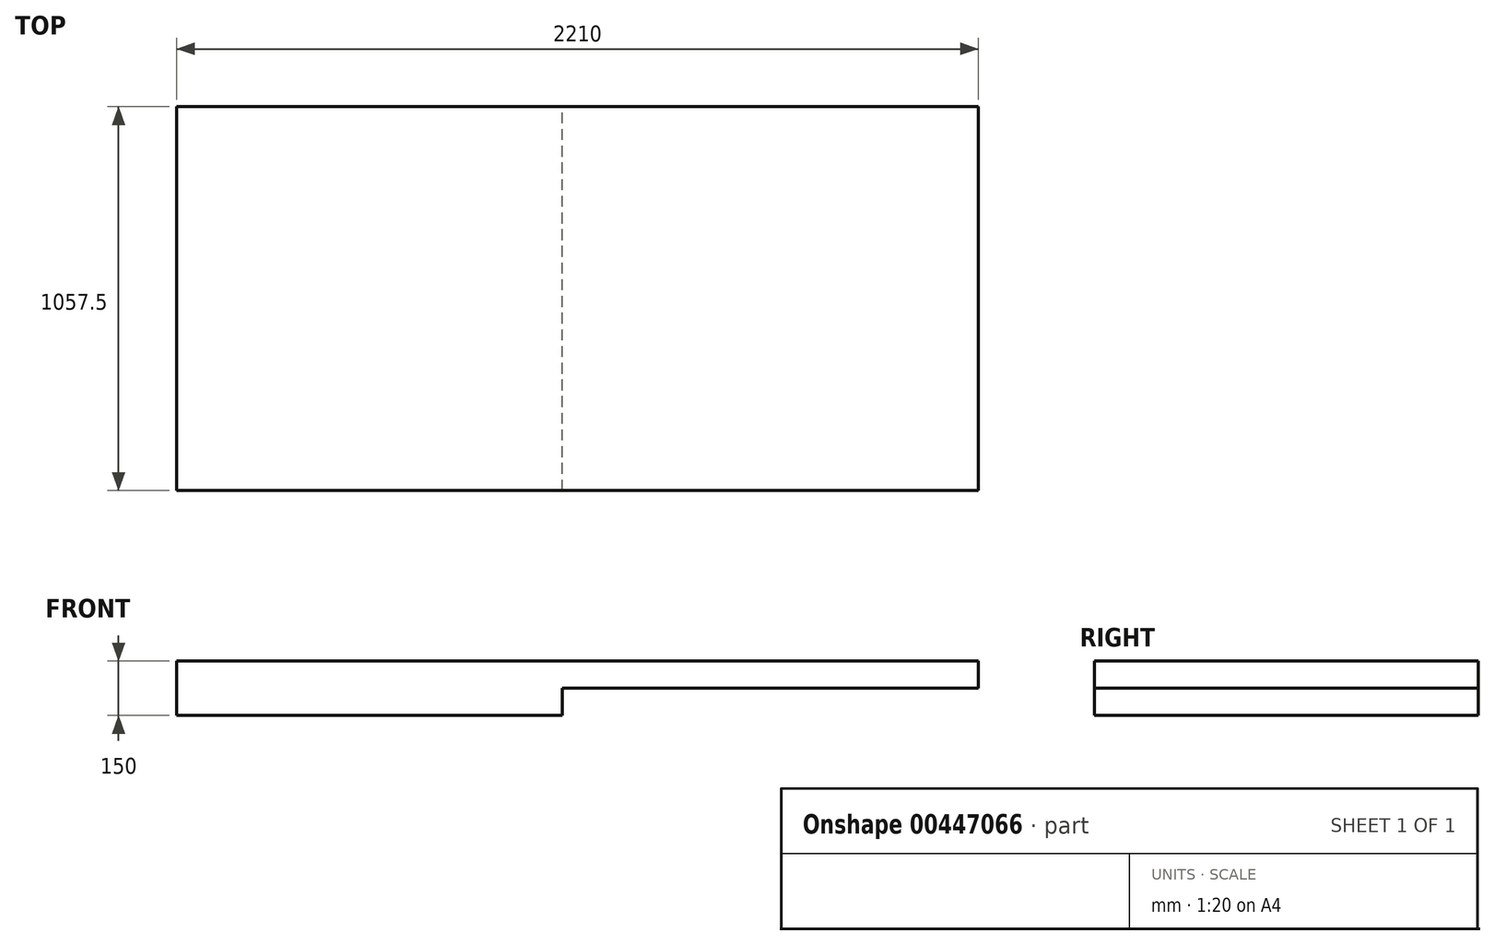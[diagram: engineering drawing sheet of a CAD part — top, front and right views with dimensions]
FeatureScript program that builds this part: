
annotation { "Feature Type Name" : "Feature", "Feature Type Description" : "" }
export const myFeature = defineFeature(function(context is Context, id is Id, definition is map)
    precondition{}
    {
        {
            var Q0;
            Q0=qCreatedBy(makeId("Top.planeOp"),FACE);
            var sketch = newSketch(context, id + "F0", { "sketchPlane" : qUnion([Q0])});
            skLineSegment(sketch, "E0.bottom", {"start": v(0, 0) * mm, "end": v(2210, 0) * mm});
            skLineSegment(sketch, "E0.top", {"start": v(0, 1057.5) * mm, "end": v(2210, 1057.5) * mm});
            skLineSegment(sketch, "E0.left", {"start": v(0, 0) * mm, "end": v(0, 1057.5) * mm});
            skLineSegment(sketch, "E0.right", {"start": v(2210, 0) * mm, "end": v(2210, 1057.5) * mm});
            skSolve(sketch);
        }
        {
            var Q0;
            Q0=makeQuery(id+"F0.imprint","IMPRINT",FACE,{"disambiguationData":[TD([[makeQuery(id+"F0.imprint","IMPRINT",EDGE,{"derivedFrom":sQuery(id+"F0.wireOp",EDGE,"E0.bottom")}),1.0]])]});
            extrude(context, id + "F1", {"entities" : qUnion([Q0]), "depth" : (65 * 2 + 20) * mm, "offsetDistance" : 25 * mm});
        }
        {
            var Q0;
            Q0=makeQuery(id+"F1.opExtrude","CAP_FACE",FACE,{"disambiguationData":[OSD([sQuery(id+"F0.wireOp",EDGE,"E0.bottom"),sQuery(id+"F0.wireOp",EDGE,"E0.top"),sQuery(id+"F0.wireOp",EDGE,"E0.left"),sQuery(id+"F0.wireOp",EDGE,"E0.right")])],"isStart":true});
            var sketch = newSketch(context, id + "F2", { "sketchPlane" : qUnion([Q0])});
            skLineSegment(sketch, "E1", {"start": v(1062.5, 0) * mm, "end": v(1062.5, -1057.5) * mm});
            skSolve(sketch);
        }
        {
            var Q0;
            {var subQ0=sQuery(id+"F2.wireOp",EDGE,"E1");Q0=makeQuery(id+"F2.imprint","IMPRINT",FACE,{"disambiguationData":[TD([[makeQuery(id+"F2.imprint","IMPRINT",EDGE,{"derivedFrom":subQ0}),1.0]])]});}
            extrude(context, id + "F3", {"entities" : qUnion([Q0]), "operationType" : NewBodyOperationType.REMOVE, "oppositeDirection" : true, "depth" : (150 - 65 - 10) * mm, "offsetDistance" : 25 * mm});
        }
    });
